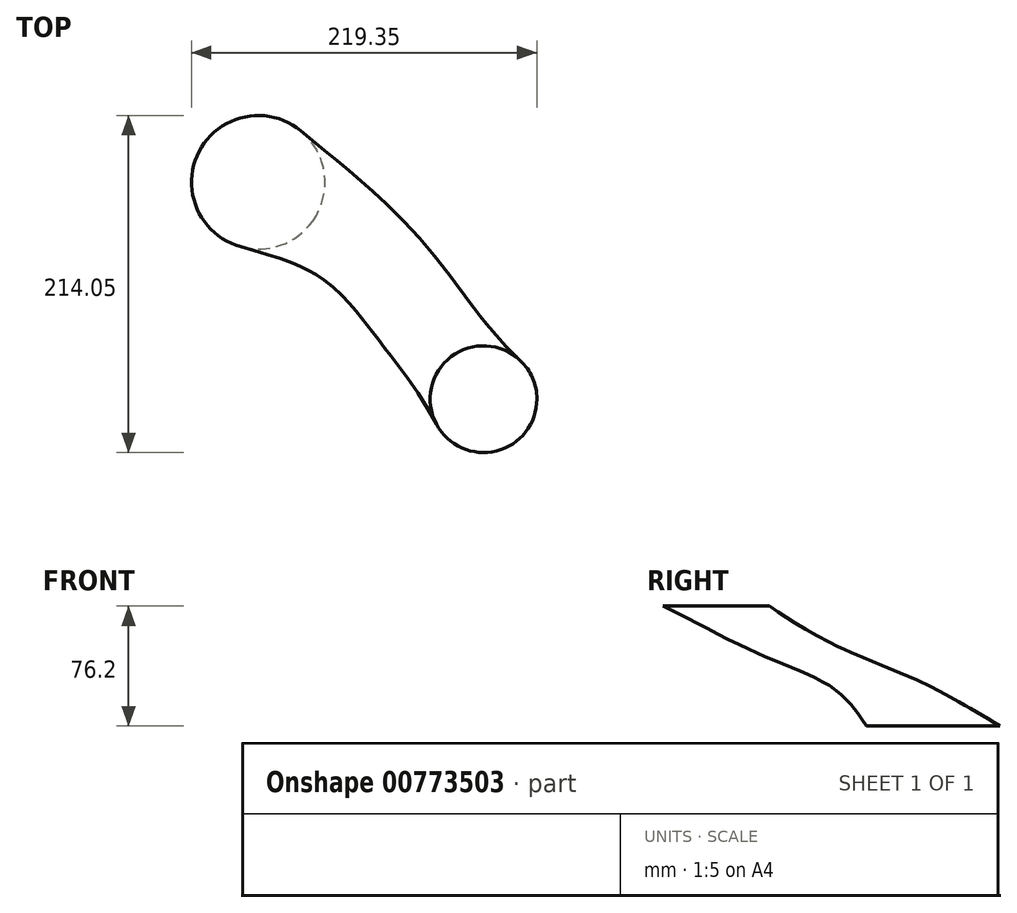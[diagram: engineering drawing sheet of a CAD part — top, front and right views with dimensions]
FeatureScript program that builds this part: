
annotation { "Feature Type Name" : "Feature", "Feature Type Description" : "" }
export const myFeature = defineFeature(function(context is Context, id is Id, definition is map)
    precondition{}
    {
        {
            var Q0;
            Q0=qCreatedBy(makeId("Top.planeOp"),FACE);
            cPlane(context, id + "F0", {"entities" : qUnion([Q0]), "cplaneType" : CPlaneType.OFFSET, "offset" : 25.4 * mm, "width" : 152.4 * mm, "height" : 152.4 * mm});
        }
        {
            var Q0;
            Q0=qCreatedBy(id+"F0.planeOp",FACE);
            cPlane(context, id + "F1", {"entities" : qUnion([Q0]), "cplaneType" : CPlaneType.OFFSET, "offset" : 25.4 * mm, "width" : 152.4 * mm, "height" : 152.4 * mm});
        }
        {
            var Q0;
            Q0=qCreatedBy(id+"F1.planeOp",FACE);
            cPlane(context, id + "F2", {"entities" : qUnion([Q0]), "cplaneType" : CPlaneType.OFFSET, "offset" : 25.4 * mm, "width" : 152.4 * mm, "height" : 152.4 * mm});
        }
        {
            var Q0;
            Q0=qCreatedBy(id+"F2.planeOp",FACE);
            cPlane(context, id + "F3", {"entities" : qUnion([Q0]), "cplaneType" : CPlaneType.OFFSET, "offset" : 25.4 * mm, "width" : 152.4 * mm, "height" : 152.4 * mm});
        }
        {
            var Q0;
            Q0=qCreatedBy(id+"F3.planeOp",FACE);
            var sketch = newSketch(context, id + "F4", { "sketchPlane" : qUnion([Q0])});
            skCircle(sketch, "E0", {"center": v(56.71, -55.7) * mm, "radius": 33.9 * mm});
            skSolve(sketch);
        }
        {
            var Q0;
            Q0=qCreatedBy(id+"F2.planeOp",FACE);
            var sketch = newSketch(context, id + "F5", { "sketchPlane" : qUnion([Q0])});
            skCircle(sketch, "E1", {"center": v(21.42, -9.2) * mm, "radius": 30.28 * mm});
            skSolve(sketch);
        }
        {
            var Q0;
            Q0=qCreatedBy(id+"F1.planeOp",FACE);
            var sketch = newSketch(context, id + "F6", { "sketchPlane" : qUnion([Q0])});
            skCircle(sketch, "E2", {"center": v(-29.48, 48) * mm, "radius": 31.55 * mm});
            skSolve(sketch);
        }
        {
            var Q0;
            Q0=qCreatedBy(id+"F0.planeOp",FACE);
            var sketch = newSketch(context, id + "F7", { "sketchPlane" : qUnion([Q0])});
            skCircle(sketch, "E3", {"center": v(-86.32, 82.02) * mm, "radius": 42.41 * mm});
            skSolve(sketch);
        }
        {
            var Q0;
            Q0 = qSketchRegion(id + "F4", true);
            var Q1;
            Q1=makeQuery(id+"F5.imprint","IMPRINT",FACE,{"disambiguationData":[TD([[makeQuery(id+"F5.imprint","IMPRINT",EDGE,{"derivedFrom":sQuery(id+"F5.wireOp",EDGE,"E1")}),1.0]])]});
            var Q2;
            Q2=makeQuery(id+"F6.imprint","IMPRINT",FACE,{"disambiguationData":[TD([[makeQuery(id+"F6.imprint","IMPRINT",EDGE,{"derivedFrom":sQuery(id+"F6.wireOp",EDGE,"E2")}),1.0]])]});
            var Q3;
            Q3=makeQuery(id+"F7.imprint","IMPRINT",FACE,{"disambiguationData":[TD([[makeQuery(id+"F7.imprint","IMPRINT",EDGE,{"derivedFrom":sQuery(id+"F7.wireOp",EDGE,"E3")}),1.0]])]});
            loft(context, id + "F8", {"sheetProfilesArray" : [{ "sheetProfileEntities" : qUnion([Q0]) }, { "sheetProfileEntities" : qUnion([Q1]) }, { "sheetProfileEntities" : qUnion([Q2]) }, { "sheetProfileEntities" : qUnion([Q3]) }]});
        }
    });
